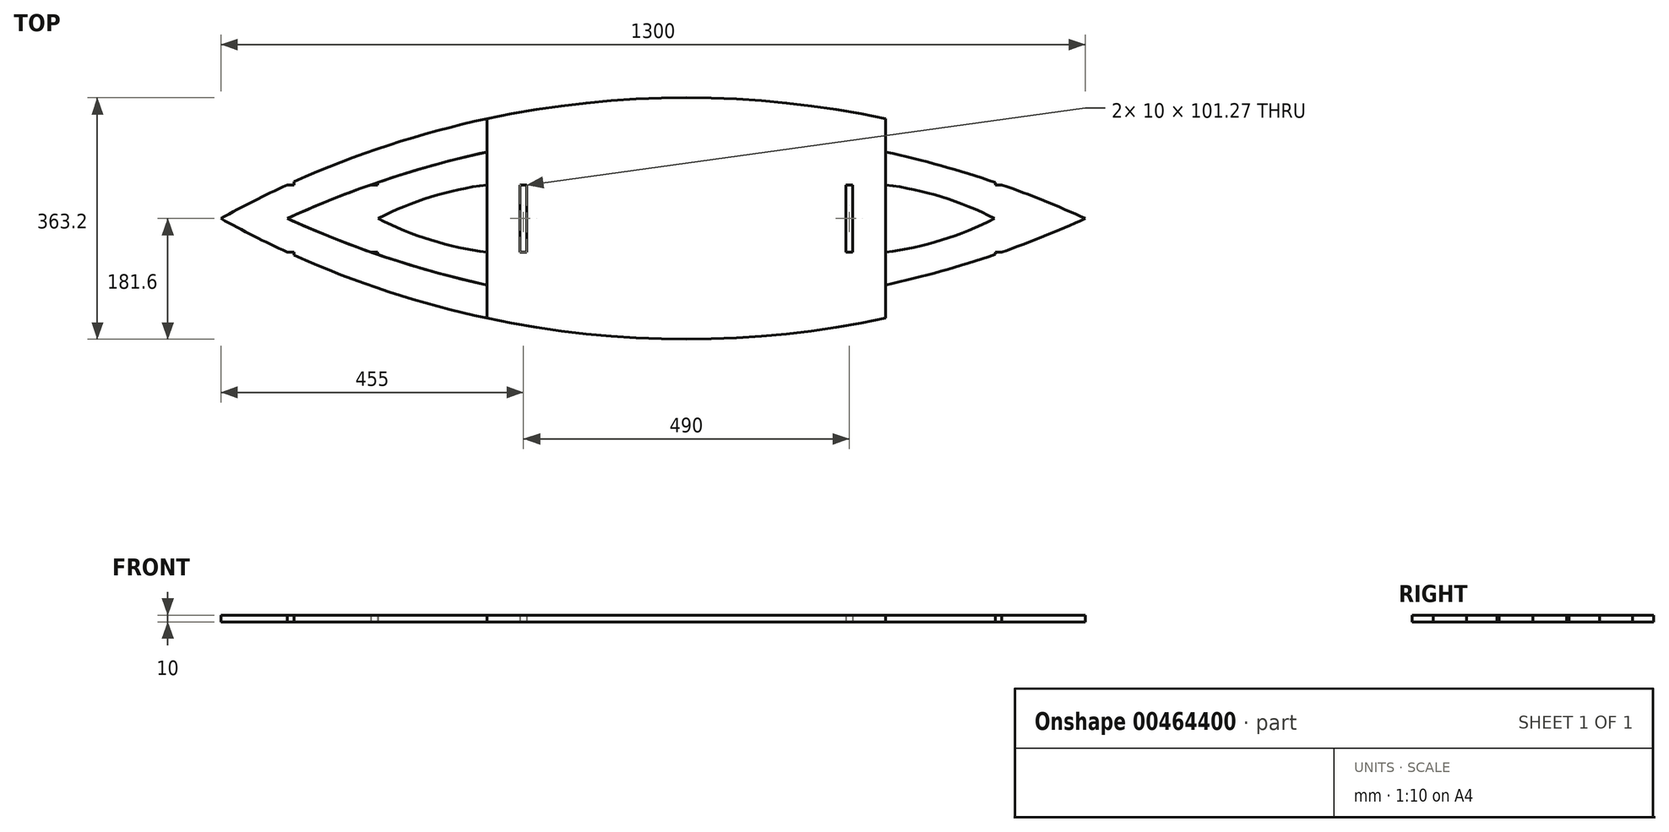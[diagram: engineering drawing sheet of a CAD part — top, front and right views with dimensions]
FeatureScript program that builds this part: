
annotation { "Feature Type Name" : "Feature", "Feature Type Description" : "" }
export const myFeature = defineFeature(function(context is Context, id is Id, definition is map)
    precondition{}
    {
        {
            var Q0;
            Q0=qCreatedBy(makeId("Top.planeOp"),FACE);
            var sketch = newSketch(context, id + "F0", { "sketchPlane" : qUnion([Q0])});
            skLineSegment(sketch, "E0", {"start": v(-1628.52, 0) * mm, "end": v(1582.02, 0) * mm, "construction": true});
            skLineSegment(sketch, "E1", {"start": v(0, 1146) * mm, "end": v(0, -696.99) * mm, "construction": true});
            skLineSegment(sketch, "E2.bottom", {"start": v(300, 150) * mm, "end": v(-300, 150) * mm, "construction": true});
            skLineSegment(sketch, "E2.top", {"start": v(300, -150) * mm, "end": v(-300, -150) * mm, "construction": true});
            skLineSegment(sketch, "E2.left", {"start": v(300, 150) * mm, "end": v(300, -150) * mm});
            skLineSegment(sketch, "E2.right", {"start": v(-300, 150) * mm, "end": v(-300, -150) * mm});
            skPoint(sketch, "E2.middle", {"position": v(0, 0) * mm});
            skCircle(sketch, "E3", {"center": v(0, -1258.33) * mm, "radius": 1439.93 * mm});
            skPoint(sketch, "E3.first.point", {"position": v(-700, 0) * mm});
            skCircle(sketch, "E4", {"center": v(0, 1258.33) * mm, "radius": 1439.93 * mm});
            skLineSegment(sketch, "E5", {"start": v(-600, 351.04) * mm, "end": v(-600, -576.85) * mm, "construction": true});
            skLineSegment(sketch, "E6", {"start": v(-600, 50.64) * mm, "end": v(-487.72, 50.64) * mm, "construction": true});
            skLineSegment(sketch, "E7", {"start": v(-600, -50.64) * mm, "end": v(600, -50.64) * mm, "construction": true});
            skLineSegment(sketch, "E8", {"start": v(-250, 50.64) * mm, "end": v(-250, -50.64) * mm});
            skLineSegment(sketch, "E9", {"start": v(-250, 50.64) * mm, "end": v(-240, 50.64) * mm});
            skLineSegment(sketch, "E10", {"start": v(-240, 50.64) * mm, "end": v(-240, -50.64) * mm});
            skLineSegment(sketch, "E11", {"start": v(-240, -50.64) * mm, "end": v(-250, -50.64) * mm});
            skLineSegment(sketch, "E12", {"start": v(-300, 150) * mm, "end": v(-300, 100) * mm, "construction": true});
            skArc(sketch, "E13", {"start": v(-300, 100) * mm, "mid": v(-452.7, 58.09) * mm, "end": v(-600, 0) * mm});
            skArc(sketch, "E14.MirrorCS", {"start": v(-300, -100) * mm, "mid": v(-452.7, -58.09) * mm, "end": v(-600, 0) * mm});
            skArc(sketch, "E15.MirrorCS", {"start": v(300, 100) * mm, "mid": v(452.7, 58.09) * mm, "end": v(600, 0) * mm});
            skArc(sketch, "E16.MirrorCS", {"start": v(300, -100) * mm, "mid": v(452.7, -58.09) * mm, "end": v(600, 0) * mm});
            skLineSegment(sketch, "E17.MirrorCS", {"start": v(250, 50.64) * mm, "end": v(240, 50.64) * mm});
            skLineSegment(sketch, "E18.MirrorCS", {"start": v(240, -50.64) * mm, "end": v(250, -50.64) * mm});
            skLineSegment(sketch, "E19.MirrorCS", {"start": v(240, 50.64) * mm, "end": v(240, -50.64) * mm});
            skLineSegment(sketch, "E20.MirrorCS", {"start": v(250, 50.64) * mm, "end": v(250, -50.64) * mm});
            skLineSegment(sketch, "E21", {"start": v(-590, 50.64) * mm, "end": v(-590, -50.64) * mm, "construction": true});
            skLineSegment(sketch, "E22", {"start": v(-600, 50.64) * mm, "end": v(-590, 50.64) * mm});
            skLineSegment(sketch, "E23", {"start": v(-590, 55.17) * mm, "end": v(-590, 50.64) * mm});
            skLineSegment(sketch, "E24", {"start": v(-600, -50.64) * mm, "end": v(-590, -50.64) * mm});
            skLineSegment(sketch, "E25", {"start": v(-590, -50.64) * mm, "end": v(-590, -55.17) * mm});
            skLineSegment(sketch, "E26.MirrorCS", {"start": v(600, -50.64) * mm, "end": v(590, -50.64) * mm});
            skLineSegment(sketch, "E27.MirrorCS", {"start": v(590, -50.64) * mm, "end": v(590, -55.17) * mm});
            skLineSegment(sketch, "E28.MirrorCS", {"start": v(590, 55.17) * mm, "end": v(590, 50.64) * mm});
            skLineSegment(sketch, "E29.MirrorCS", {"start": v(600, 50.64) * mm, "end": v(590, 50.64) * mm});
            skArc(sketch, "E30", {"start": v(-300, 50.64) * mm, "mid": v(-383.99, 32.46) * mm, "end": v(-463.55, 0) * mm});
            skArc(sketch, "E31.MirrorCS", {"start": v(-300, -50.64) * mm, "mid": v(-383.99, -32.46) * mm, "end": v(-463.55, 0) * mm});
            skArc(sketch, "E32.MirrorCS", {"start": v(300, 50.64) * mm, "mid": v(383.99, 32.46) * mm, "end": v(463.55, 0) * mm});
            skArc(sketch, "E33.MirrorCS", {"start": v(300, -50.64) * mm, "mid": v(383.99, -32.46) * mm, "end": v(463.55, 0) * mm});
            skLineSegment(sketch, "E34", {"start": v(-474.47, 50.64) * mm, "end": v(-464.47, 50.64) * mm});
            skLineSegment(sketch, "E35.trimOffspring", {"start": v(-474.47, 50.64) * mm, "end": v(600, 50.64) * mm, "construction": true});
            skLineSegment(sketch, "E36", {"start": v(-464.47, 50.64) * mm, "end": v(-464.47, 67.59) * mm});
            skLineSegment(sketch, "E37.MirrorCS", {"start": v(-464.47, -50.64) * mm, "end": v(-464.47, -67.59) * mm});
            skLineSegment(sketch, "E38.MirrorCS", {"start": v(-474.47, -50.64) * mm, "end": v(-464.47, -50.64) * mm});
            skLineSegment(sketch, "E39.MirrorCS", {"start": v(464.47, -50.64) * mm, "end": v(464.47, -67.59) * mm});
            skLineSegment(sketch, "E40.MirrorCS", {"start": v(474.47, 50.64) * mm, "end": v(464.47, 50.64) * mm});
            skLineSegment(sketch, "E41.MirrorCS", {"start": v(474.47, -50.64) * mm, "end": v(464.47, -50.64) * mm});
            skLineSegment(sketch, "E42.MirrorCS", {"start": v(464.47, 50.64) * mm, "end": v(464.47, 67.59) * mm});
            skPoint(sketch, "E43", {"position": v(700, 0) * mm});
            skSolve(sketch);
        }
        {
            var Q0;
            {var subQ10=sQuery(id+"F0.wireOp",EDGE,"E15.MirrorCS");Q0=makeQuery(id+"F0.imprint","IMPRINT",FACE,{"disambiguationData":[TD([[makeQuery(id+"F0.imprint","IMPRINT",EDGE,{"derivedFrom":subQ10}),1.0]])]});}
            var Q1;
            {var subQ5=sQuery(id+"F0.wireOp",EDGE,"E13");Q1=makeQuery(id+"F0.imprint","IMPRINT",FACE,{"disambiguationData":[TD([[makeQuery(id+"F0.imprint","IMPRINT",EDGE,{"derivedFrom":subQ5}),-1.0]])]});}
            extrude(context, id + "F1", {"entities" : qUnion([Q0, Q1]), "depth" : 10 * mm});
        }
        {
            var Q0;
            Q0=makeQuery(id+"F0.imprint","IMPRINT",FACE,{"disambiguationData":[TD([[makeQuery(id+"F0.imprint","IMPRINT",EDGE,{"derivedFrom":sQuery(id+"F0.wireOp",EDGE,"E8")}),-1.0]])]});
            extrude(context, id + "F2", {"entities" : qUnion([Q0]), "depth" : 10 * mm});
        }
        {
            var Q0;
            {var subQ13=sQuery(id+"F0.wireOp",EDGE,"E30");Q0=makeQuery(id+"F0.imprint","IMPRINT",FACE,{"disambiguationData":[TD([[makeQuery(id+"F0.imprint","IMPRINT",EDGE,{"derivedFrom":subQ13}),-1.0]])]});}
            var Q1;
            {var subQ10=sQuery(id+"F0.wireOp",EDGE,"E32.MirrorCS");Q1=makeQuery(id+"F0.imprint","IMPRINT",FACE,{"disambiguationData":[TD([[makeQuery(id+"F0.imprint","IMPRINT",EDGE,{"derivedFrom":subQ10}),1.0]])]});}
            extrude(context, id + "F3", {"entities" : qUnion([Q0, Q1]), "depth" : 10 * mm});
        }
    });
